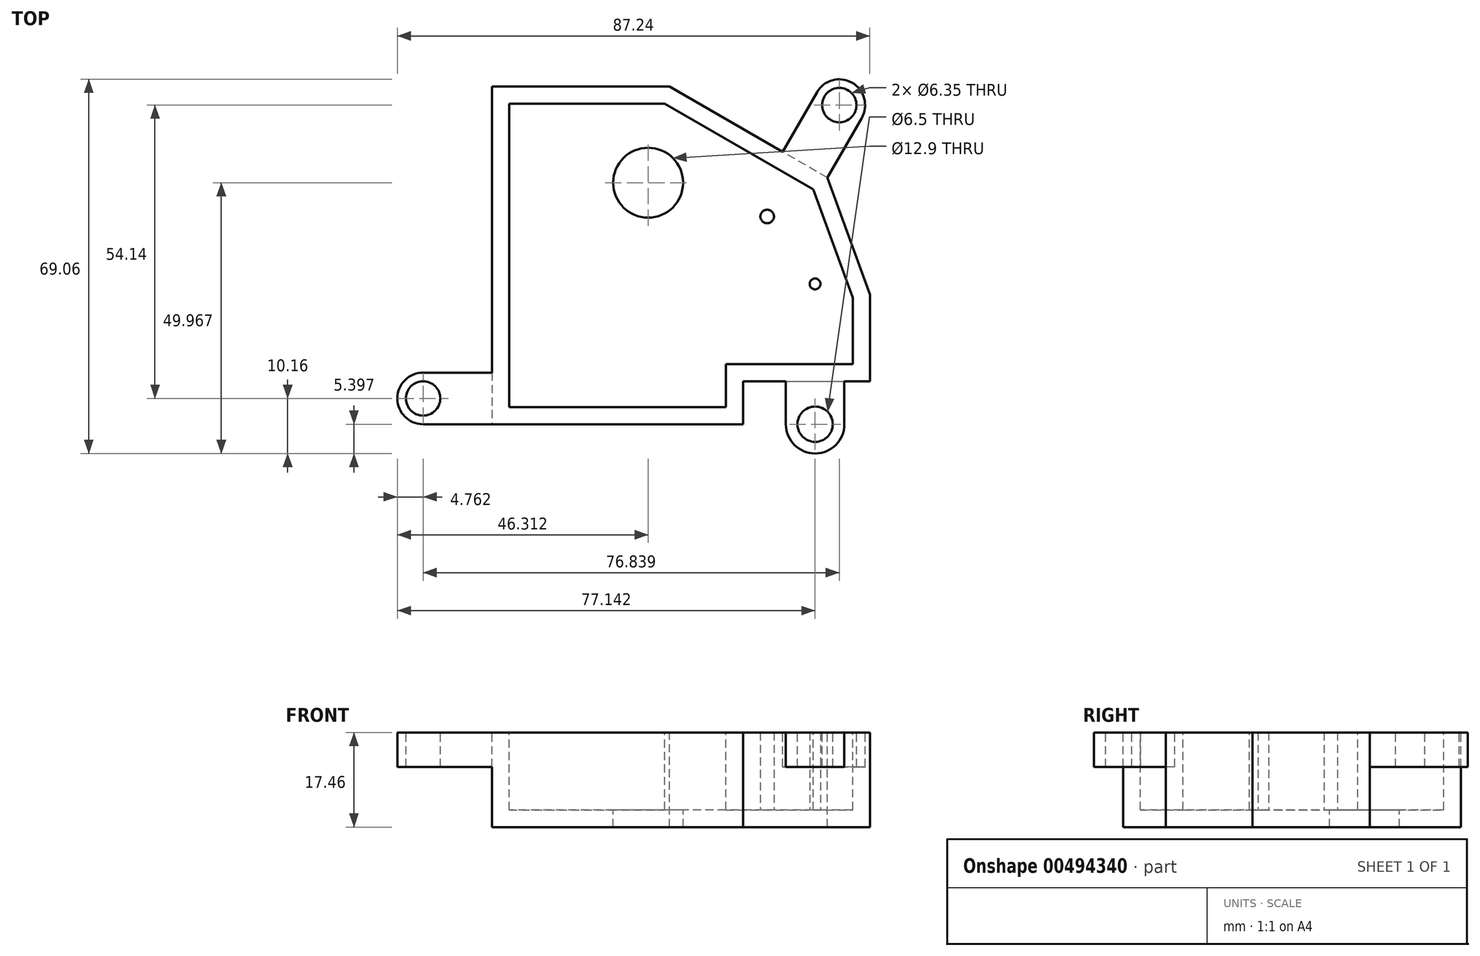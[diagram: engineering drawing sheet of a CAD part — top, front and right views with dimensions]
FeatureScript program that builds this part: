
annotation { "Feature Type Name" : "Feature", "Feature Type Description" : "" }
export const myFeature = defineFeature(function(context is Context, id is Id, definition is map)
    precondition{}
    {
        {
            var Q0;
            Q0=qCreatedBy(makeId("Top.planeOp"),FACE);
            var sketch = newSketch(context, id + "F0", { "sketchPlane" : qUnion([Q0])});
            skLineSegment(sketch, "E0.top", {"start": v(13.61, -39.26) * mm, "end": v(-32.77, -39.26) * mm});
            skArc(sketch, "E1", {"start": v(-45.47, -29.74) * mm, "mid": v(-50.23, -34.5) * mm, "end": v(-45.47, -39.26) * mm});
            skLineSegment(sketch, "E2", {"start": v(-45.47, -29.74) * mm, "end": v(-32.77, -29.74) * mm});
            skLineSegment(sketch, "E3.trimOffspring", {"start": v(-32.77, 23.09) * mm, "end": v(-32.77, -29.74) * mm});
            skLineSegment(sketch, "E4", {"start": v(-45.47, -39.26) * mm, "end": v(-32.77, -39.26) * mm});
            skLineSegment(sketch, "E5", {"start": v(13.61, -39.26) * mm, "end": v(13.61, -31.36) * mm});
            skLineSegment(sketch, "E6", {"start": v(13.61, -31.36) * mm, "end": v(21.51, -31.36) * mm});
            skLineSegment(sketch, "E7", {"start": v(21.51, -31.36) * mm, "end": v(21.51, -39.26) * mm});
            skLineSegment(sketch, "E8", {"start": v(37.01, -31.36) * mm, "end": v(37.01, -15.35) * mm});
            skLineSegment(sketch, "E9", {"start": v(-32.77, 23.09) * mm, "end": v(0, 23.09) * mm});
            skLineSegment(sketch, "E10", {"start": v(37.01, -15.35) * mm, "end": v(29.15, 6.26) * mm});
            skLineSegment(sketch, "E11", {"start": v(20.9, 11.02) * mm, "end": v(0, 23.09) * mm});
            skLineSegment(sketch, "E12", {"start": v(29.15, 6.26) * mm, "end": v(35.5, 17.26) * mm});
            skLineSegment(sketch, "E13", {"start": v(20.9, 11.02) * mm, "end": v(27.25, 22.02) * mm});
            skArc(sketch, "E14", {"start": v(35.5, 17.26) * mm, "mid": v(33.75, 23.76) * mm, "end": v(27.25, 22.02) * mm});
            skCircle(sketch, "E15", {"center": v(31.37, 19.64) * mm, "radius": 3.17 * mm});
            skCircle(sketch, "E16", {"center": v(26.91, -39.26) * mm, "radius": 3.25 * mm});
            skCircle(sketch, "E17", {"center": v(-45.47, -34.5) * mm, "radius": 3.17 * mm});
            skLineSegment(sketch, "E18", {"start": v(-32.77, -29.74) * mm, "end": v(-32.77, -39.26) * mm});
            skLineSegment(sketch, "E19", {"start": v(21.51, -31.36) * mm, "end": v(37.01, -31.36) * mm});
            skLineSegment(sketch, "E20", {"start": v(29.15, 6.26) * mm, "end": v(20.9, 11.02) * mm});
            skArc(sketch, "E21", {"start": v(21.51, -39.26) * mm, "mid": v(26.91, -44.66) * mm, "end": v(32.31, -39.26) * mm});
            skLineSegment(sketch, "E22", {"start": v(32.31, -39.26) * mm, "end": v(32.31, -31.36) * mm});
            skSolve(sketch);
        }
        {
            var Q0;
            Q0=makeQuery(id+"F0.imprint","IMPRINT",FACE,{"disambiguationData":[TD([[makeQuery(id+"F0.imprint","IMPRINT",EDGE,{"derivedFrom":sQuery(id+"F0.wireOp",EDGE,"E0.top")}),-1.0]])]});
            extrude(context, id + "F1", {"entities" : qUnion([Q0]), "oppositeDirection" : true, "depth" : 17.46 * mm, "offsetDistance" : 25.4 * mm});
        }
        {
            var Q0;
            Q0=makeQuery(id+"F1.opExtrude","CAP_FACE",FACE,{"disambiguationData":[OSD([sQuery(id+"F0.wireOp",EDGE,"E0.top"),sQuery(id+"F0.wireOp",EDGE,"E3.trimOffspring"),sQuery(id+"F0.wireOp",EDGE,"E5"),sQuery(id+"F0.wireOp",EDGE,"E6"),sQuery(id+"F0.wireOp",EDGE,"E8"),sQuery(id+"F0.wireOp",EDGE,"E9"),sQuery(id+"F0.wireOp",EDGE,"E10"),sQuery(id+"F0.wireOp",EDGE,"E11"),sQuery(id+"F0.wireOp",EDGE,"E18"),sQuery(id+"F0.wireOp",EDGE,"E19"),sQuery(id+"F0.wireOp",EDGE,"E20")])],"isStart":true});
            shell(context, id + "F2", {"entities" : qUnion([Q0]), "thickness" : 3.17 * mm});
        }
        {
            var Q0;
            Q0=makeQuery(id+"F0.imprint","IMPRINT",FACE,{"disambiguationData":[TD([[makeQuery(id+"F0.imprint","IMPRINT",EDGE,{"derivedFrom":sQuery(id+"F0.wireOp",EDGE,"E1")}),1.0]])]});
            var Q1;
            {var subQ1=sQuery(id+"F0.wireOp",EDGE,"65bNLONK-Gj9D-9pQx-jRsf-sQ69z0gVqBZc");Q1=makeQuery(id+"F0.imprint","IMPRINT",FACE,{"disambiguationData":[TD([[makeQuery(id+"F0.imprint","IMPRINT",EDGE,{"derivedFrom":subQ1}),1.0]])]});}
            var Q2;
            Q2=makeQuery(id+"F0.imprint","IMPRINT",FACE,{"disambiguationData":[TD([[makeQuery(id+"F0.imprint","IMPRINT",EDGE,{"derivedFrom":sQuery(id+"F0.wireOp",EDGE,"E12")}),1.0]])]});
            var Q3;
            {var subQ1=sQuery(id+"F0.wireOp",EDGE,"E7");Q3=makeQuery(id+"F0.imprint","IMPRINT",FACE,{"disambiguationData":[TD([[makeQuery(id+"F0.imprint","IMPRINT",EDGE,{"derivedFrom":subQ1}),1.0]])]});}
            extrude(context, id + "F3", {"entities" : qUnion([Q0, Q1, Q2, Q3]), "operationType" : NewBodyOperationType.ADD, "oppositeDirection" : true, "depth" : 6.35 * mm, "offsetDistance" : 25.4 * mm});
        }
        {
            var Q0;
            Q0=makeQuery(id+"F2.opShell","OFFSET_FACE",FACE,{"disambiguationData":[OSD([sQuery(id+"F0.wireOp",EDGE,"E0.top"),sQuery(id+"F0.wireOp",EDGE,"E3.trimOffspring"),sQuery(id+"F0.wireOp",EDGE,"E5"),sQuery(id+"F0.wireOp",EDGE,"E6"),sQuery(id+"F0.wireOp",EDGE,"E8"),sQuery(id+"F0.wireOp",EDGE,"E9"),sQuery(id+"F0.wireOp",EDGE,"E10"),sQuery(id+"F0.wireOp",EDGE,"E11"),sQuery(id+"F0.wireOp",EDGE,"E18"),sQuery(id+"F0.wireOp",EDGE,"E19"),sQuery(id+"F0.wireOp",EDGE,"E20")])]});
            var sketch = newSketch(context, id + "F4", { "sketchPlane" : qUnion([Q0])});
            skCircle(sketch, "E23", {"center": v(26.9, -13.37) * mm, "radius": 1 * mm});
            skCircle(sketch, "E24", {"center": v(18.06, -0.92) * mm, "radius": 1.25 * mm});
            skCircle(sketch, "E25", {"center": v(-3.92, 5.3) * mm, "radius": 6.45 * mm});
            skSolve(sketch);
        }
        {
            var Q0;
            Q0=makeQuery(id+"F4.imprint","IMPRINT",FACE,{"disambiguationData":[TD([[makeQuery(id+"F4.imprint","IMPRINT",EDGE,{"derivedFrom":sQuery(id+"F4.wireOp",EDGE,"E23")}),1.0]])]});
            var Q1;
            Q1=makeQuery(id+"F4.imprint","IMPRINT",FACE,{"disambiguationData":[TD([[makeQuery(id+"F4.imprint","IMPRINT",EDGE,{"derivedFrom":sQuery(id+"F4.wireOp",EDGE,"E24")}),1.0]])]});
            var Q2;
            {var subQ0=sQuery(id+"F0.wireOp",EDGE,"E20");var subQ1=sQuery(id+"F0.wireOp",EDGE,"E19");var subQ2=sQuery(id+"F0.wireOp",EDGE,"E8");var subQ3=sQuery(id+"F0.wireOp",EDGE,"E18");Q2=makeQuery(id+"F3.boolean.opBoolean","MERGE",FACE,{"derivedFrom":[makeQuery(id+"F1.opExtrude","CAP_FACE",FACE,{"disambiguationData":[OSD([sQuery(id+"F0.wireOp",EDGE,"E0.top"),sQuery(id+"F0.wireOp",EDGE,"E3.trimOffspring"),sQuery(id+"F0.wireOp",EDGE,"E5"),sQuery(id+"F0.wireOp",EDGE,"E6"),subQ2,sQuery(id+"F0.wireOp",EDGE,"E9"),sQuery(id+"F0.wireOp",EDGE,"E10"),sQuery(id+"F0.wireOp",EDGE,"E11"),subQ3,subQ1,subQ0])],"isStart":true}),makeQuery(id+"F3.opExtrude","CAP_FACE",FACE,{"disambiguationData":[OSD([sQuery(id+"F0.wireOp",EDGE,"E1"),sQuery(id+"F0.wireOp",EDGE,"E2"),sQuery(id+"F0.wireOp",EDGE,"E4"),sQuery(id+"F0.wireOp",EDGE,"E17"),subQ3])],"isStart":true}),makeQuery(id+"F3.opExtrude","CAP_FACE",FACE,{"disambiguationData":[OSD([sQuery(id+"F0.wireOp",EDGE,"65bNLONK-Gj9D-9pQx-jRsf-sQ69z0gVqBZc"),sQuery(id+"F0.wireOp",EDGE,"E7"),subQ2,sQuery(id+"F0.wireOp",EDGE,"E16"),subQ1])],"isStart":true}),makeQuery(id+"F3.opExtrude","CAP_FACE",FACE,{"disambiguationData":[OSD([sQuery(id+"F0.wireOp",EDGE,"E12"),sQuery(id+"F0.wireOp",EDGE,"E13"),sQuery(id+"F0.wireOp",EDGE,"E14"),sQuery(id+"F0.wireOp",EDGE,"E15"),subQ0])],"isStart":true})]});}
            extrude(context, id + "F5", {"entities" : qUnion([Q0, Q1]), "operationType" : NewBodyOperationType.ADD, "endBound" : BoundingType.UP_TO_SURFACE, "depth" : 25.4 * mm, "endBoundEntityFace" : qUnion([Q2]), "offsetDistance" : 2 * mm});
        }
        {
            var Q0;
            Q0=makeQuery(id+"F4.imprint","IMPRINT",FACE,{"disambiguationData":[TD([[makeQuery(id+"F4.imprint","IMPRINT",EDGE,{"derivedFrom":sQuery(id+"F4.wireOp",EDGE,"E25")}),1.0]])]});
            extrude(context, id + "F6", {"entities" : qUnion([Q0]), "operationType" : NewBodyOperationType.REMOVE, "endBound" : BoundingType.THROUGH_ALL, "oppositeDirection" : true, "depth" : 25.4 * mm, "offsetDistance" : 25.4 * mm});
        }
    });
